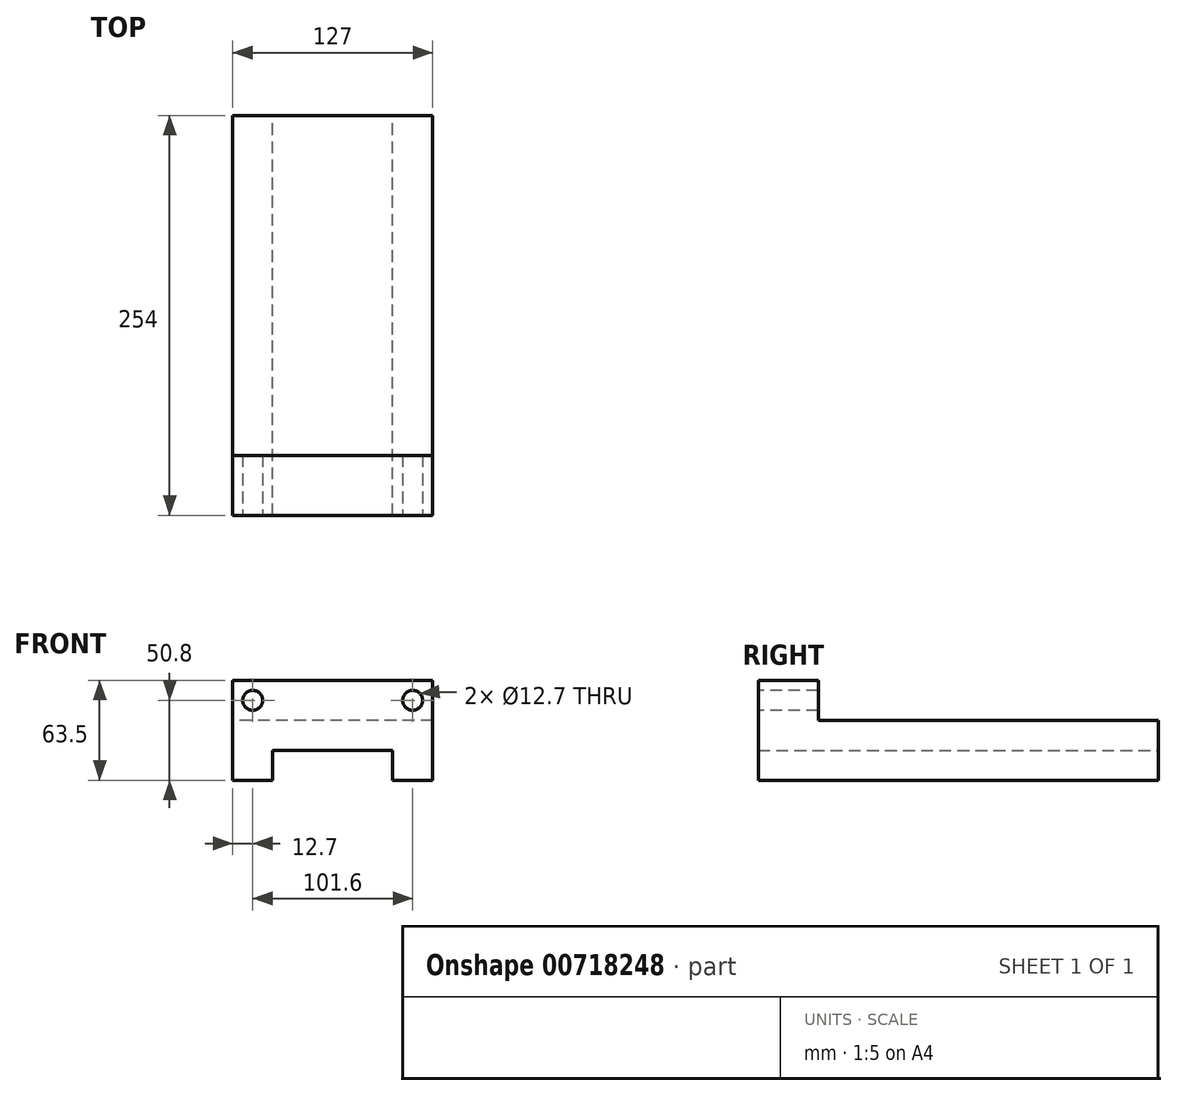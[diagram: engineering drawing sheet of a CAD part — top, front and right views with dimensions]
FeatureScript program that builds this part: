
annotation { "Feature Type Name" : "Feature", "Feature Type Description" : "" }
export const myFeature = defineFeature(function(context is Context, id is Id, definition is map)
    precondition{}
    {
        {
            var Q0;
            Q0=qCreatedBy(makeId("Right.planeOp"),FACE);
            var sketch = newSketch(context, id + "F0", { "sketchPlane" : qUnion([Q0])});
            skLineSegment(sketch, "E0", {"start": v(0, 0) * mm, "end": v(0, -63.5) * mm});
            skLineSegment(sketch, "E1", {"start": v(0, -63.5) * mm, "end": v(254, -63.5) * mm});
            skLineSegment(sketch, "E2", {"start": v(254, -63.5) * mm, "end": v(254, -25.4) * mm});
            skLineSegment(sketch, "E3", {"start": v(254, -25.4) * mm, "end": v(38.1, -25.4) * mm});
            skLineSegment(sketch, "E4", {"start": v(38.1, -25.4) * mm, "end": v(38.1, 0) * mm});
            skLineSegment(sketch, "E5", {"start": v(38.1, 0) * mm, "end": v(0, 0) * mm});
            skSolve(sketch);
        }
        {
            var Q0;
            Q0=makeQuery(id+"F0.imprint","IMPRINT",FACE,{"disambiguationData":[TD([[makeQuery(id+"F0.imprint","IMPRINT",EDGE,{"derivedFrom":sQuery(id+"F0.wireOp",EDGE,"E0")}),1.0]])]});
            extrude(context, id + "F1", {"entities" : qUnion([Q0]), "depth" : 127 * mm, "offsetDistance" : 25.4 * mm});
        }
        {
            var Q0;
            Q0=makeQuery(id+"F1.opExtrude","SWEPT_FACE",FACE,{"disambiguationData":[OSD([sQuery(id+"F0.wireOp",EDGE,"E0")])]});
            var sketch = newSketch(context, id + "F2", { "sketchPlane" : qUnion([Q0])});
            skCircle(sketch, "E6", {"center": v(12.7, -12.7) * mm, "radius": 6.35 * mm});
            skCircle(sketch, "E7", {"center": v(114.3, -12.7) * mm, "radius": 6.35 * mm});
            skSolve(sketch);
        }
        {
            var Q0;
            Q0=sQuery(id+"F2.wireOp",VERTEX,"E6.center");
            var Q1;
            Q1=makeQuery(id+"F1.opExtrude","SWEPT_BODY",BODY,{"disambiguationData":[OSD([sQuery(id+"F0.wireOp",EDGE,"E0"),sQuery(id+"F0.wireOp",EDGE,"E1"),sQuery(id+"F0.wireOp",EDGE,"E2"),sQuery(id+"F0.wireOp",EDGE,"E3"),sQuery(id+"F0.wireOp",EDGE,"E4"),sQuery(id+"F0.wireOp",EDGE,"E5")])]});
            hole(context, id + "F3", {"style" : HoleStyle.SIMPLE, "endStyle" : HoleEndStyle.BLIND, "holeDiameter" : 12.7 * mm, "majorDiameter" : 6.35 * mm, "holeDepth" : 38.1 * mm, "isTappedThrough" : true, "tappedDepth" : 12.7 * mm, "tapClearance" : 3, "locations" : qUnion([Q0]), "scope" : qUnion([Q1])});
        }
        {
            var Q0;
            Q0=makeQuery(id+"F1.opExtrude","SWEPT_FACE",FACE,{"disambiguationData":[OSD([sQuery(id+"F0.wireOp",EDGE,"E0")])]});
            var sketch = newSketch(context, id + "F4", { "sketchPlane" : qUnion([Q0])});
            skPoint(sketch, "E8", {"position": v(114.3, -12.7) * mm});
            skSolve(sketch);
        }
        {
            var Q0;
            Q0=sQuery(id+"F4.wireOp",VERTEX,"E8");
            var Q1;
            Q1=makeQuery(id+"F1.opExtrude","SWEPT_BODY",BODY,{"disambiguationData":[OSD([sQuery(id+"F0.wireOp",EDGE,"E0"),sQuery(id+"F0.wireOp",EDGE,"E1"),sQuery(id+"F0.wireOp",EDGE,"E2"),sQuery(id+"F0.wireOp",EDGE,"E3"),sQuery(id+"F0.wireOp",EDGE,"E4"),sQuery(id+"F0.wireOp",EDGE,"E5")])]});
            hole(context, id + "F5", {"style" : HoleStyle.SIMPLE, "endStyle" : HoleEndStyle.BLIND, "holeDiameter" : 12.7 * mm, "majorDiameter" : 6.35 * mm, "holeDepth" : 38.1 * mm, "isTappedThrough" : true, "tappedDepth" : 12.7 * mm, "tapClearance" : 3, "locations" : qUnion([Q0]), "scope" : qUnion([Q1])});
        }
        {
            var Q0;
            Q0=makeQuery(id+"F1.opExtrude","SWEPT_FACE",FACE,{"disambiguationData":[OSD([sQuery(id+"F0.wireOp",EDGE,"E2")])]});
            var sketch = newSketch(context, id + "F6", { "sketchPlane" : qUnion([Q0])});
            skLineSegment(sketch, "E9.bottom", {"start": v(-101.6, -63.5) * mm, "end": v(-25.4, -63.5) * mm});
            skLineSegment(sketch, "E9.top", {"start": v(-101.6, -44.45) * mm, "end": v(-25.4, -44.45) * mm});
            skLineSegment(sketch, "E9.left", {"start": v(-101.6, -63.5) * mm, "end": v(-101.6, -44.45) * mm});
            skLineSegment(sketch, "E9.right", {"start": v(-25.4, -63.5) * mm, "end": v(-25.4, -44.45) * mm});
            skSolve(sketch);
        }
        {
            var Q0;
            Q0=makeQuery(id+"F6.imprint","IMPRINT",FACE,{"disambiguationData":[TD([[makeQuery(id+"F6.imprint","IMPRINT",EDGE,{"derivedFrom":sQuery(id+"F6.wireOp",EDGE,"E9.bottom")}),1.0]])]});
            extrude(context, id + "F7", {"entities" : qUnion([Q0]), "operationType" : NewBodyOperationType.REMOVE, "endBound" : BoundingType.THROUGH_ALL, "oppositeDirection" : true, "depth" : 254 * mm, "offsetDistance" : 25.4 * mm});
        }
    });
